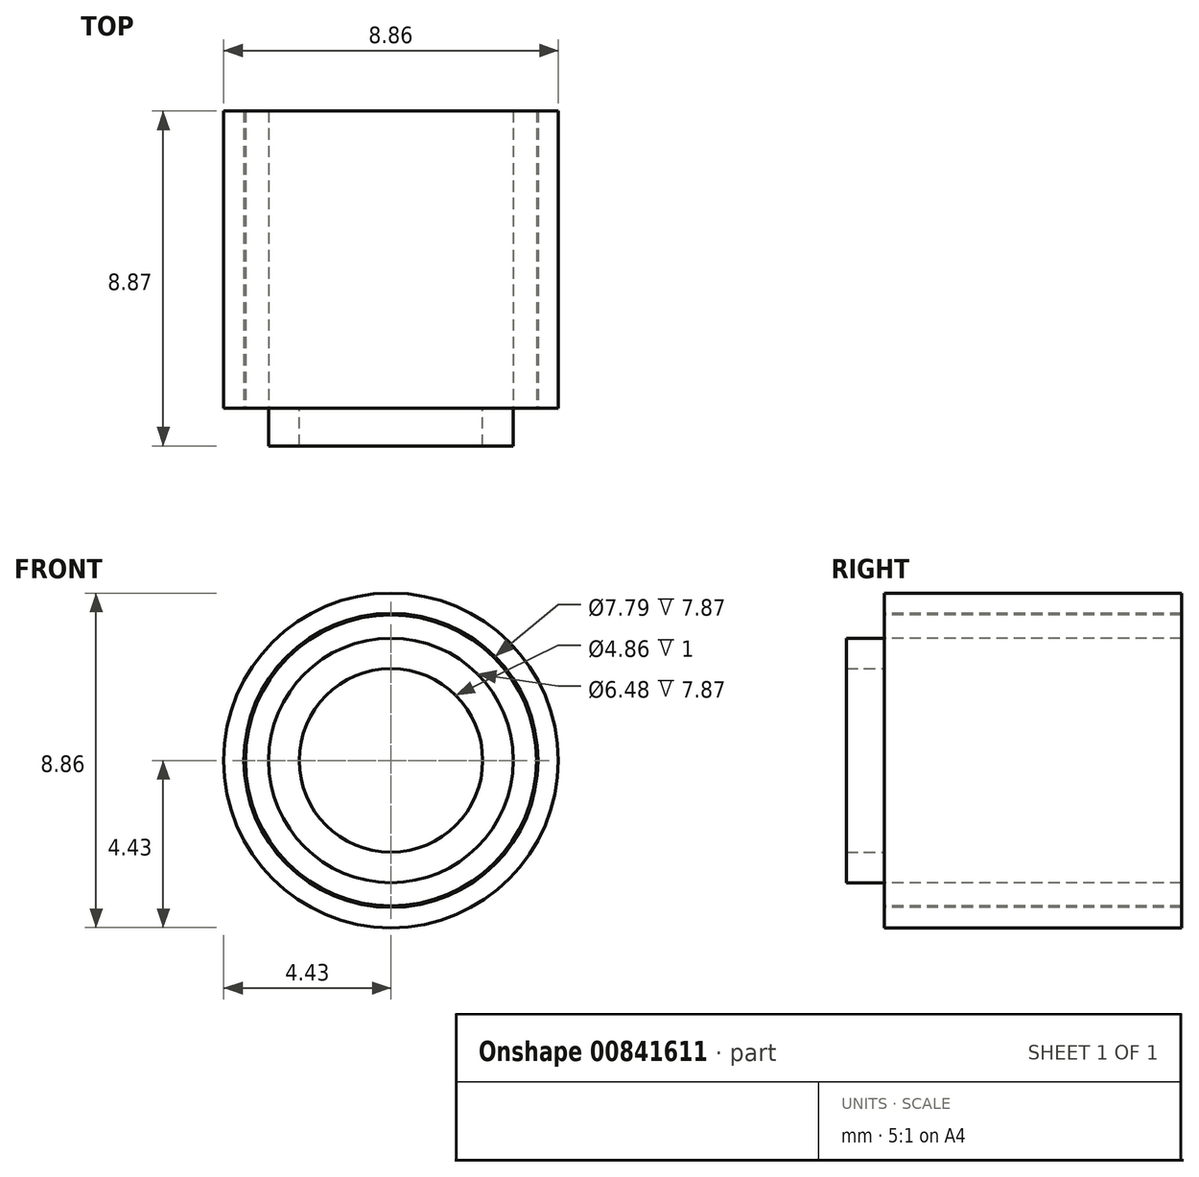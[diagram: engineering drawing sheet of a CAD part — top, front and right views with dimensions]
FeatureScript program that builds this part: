
annotation { "Feature Type Name" : "Feature", "Feature Type Description" : "" }
export const myFeature = defineFeature(function(context is Context, id is Id, definition is map)
    precondition{}
    {
        {
            var Q0;
            Q0=qCreatedBy(makeId("Front.planeOp"),FACE);
            var sketch = newSketch(context, id + "F0", { "sketchPlane" : qUnion([Q0])});
            skCircle(sketch, "E0", {"center": v(0, 0) * mm, "radius": 3.86 * mm});
            skCircle(sketch, "E1", {"center": v(0, 0) * mm, "radius": 3.9 * mm});
            skCircle(sketch, "E2", {"center": v(0, 0) * mm, "radius": 2.43 * mm});
            skCircle(sketch, "E3", {"center": v(0, 0) * mm, "radius": 3.24 * mm});
            skCircle(sketch, "E4", {"center": v(0, 0) * mm, "radius": 4.43 * mm});
            skSolve(sketch);
        }
        {
            var Q0;
            Q0=makeQuery(id+"F0.imprint","IMPRINT",FACE,{"disambiguationData":[TD([[makeQuery(id+"F0.imprint","IMPRINT",EDGE,{"derivedFrom":sQuery(id+"F0.wireOp",EDGE,"E1")}),-1.0]])]});
            var Q1;
            Q1=makeQuery(id+"F0.imprint","IMPRINT",FACE,{"disambiguationData":[TD([[makeQuery(id+"F0.imprint","IMPRINT",EDGE,{"derivedFrom":sQuery(id+"F0.wireOp",EDGE,"E0")}),1.0]])]});
            extrude(context, id + "F1", {"entities" : qUnion([Q0, Q1]), "oppositeDirection" : true, "depth" : 7.87 * mm, "offsetDistance" : 25 * mm});
        }
        {
            var Q0;
            Q0=makeQuery(id+"F0.imprint","IMPRINT",FACE,{"disambiguationData":[TD([[makeQuery(id+"F0.imprint","IMPRINT",EDGE,{"derivedFrom":sQuery(id+"F0.wireOp",EDGE,"E2")}),-1.0]])]});
            extrude(context, id + "F2", {"entities" : qUnion([Q0]), "depth" : 1 * mm, "offsetDistance" : 25 * mm});
        }
        {
            var Q0;
            Q0=sQuery(id+"F0.wireOp",EDGE,"E1");
            extrude(context, id + "F3", {"bodyType" : ToolBodyType.SURFACE, "operationType" : NewBodyOperationType.ADD, "surfaceEntities" : qUnion([Q0]), "oppositeDirection" : true, "depth" : 7.87 * mm, "offsetDistance" : 25 * mm});
        }
    });
